# Revit family: NBS_HeatraeSadia_StrgWtrHtrsElctrc_B3MC3M
name_source: partatom
category: Plumbing Fixtures
revit_build: Autodesk Revit 2014 (Build: 20130709_2115(x64)
units: mm (PartAtom-declared; Revit-internal decimal feet)

## types (2) — shared parameters
Accessories = Telescopic spout (95:970:103)
Arrangement = Single point – mains supply
AssetType = Fixed
CW Connection = Yes
CasingFinish = White stove enamel
Color = White
Connections = 15 mm copper pipe connections for cold water inlet and hot water outlet at the base of the unit, vent at the top
Controls = Valve
Depth = 352 mm  [stored 1.15486 ft]
Description = Vented point of use storage water heater
DurationUnit = year
Features = Element ‘on’ indicator, supplied complete with open outlet spout
Fixing = Wall fixed
FlowRate = To suit draw off requirements
HW Connection = No
HeatTransferSurfaceArea = 0
IfcExportAs = IfcBoilerType
IfcExportType = WATER
IsWaterStorageHeater = Yes
ManufacturerName = Heatrae Sadia
ManufacturerURL = www.heatraesadia.com
Material = Outer casing: Plastic top and bottom moulding with corrosion proof steel centre section; Water container: Heavy gauge copper; Heat unit: Replaceable embedded rod-type element sheathed in corrosion resistant alloy
NBSCertification = http://www.nationalbimlibrary.com
NBSDescription = Storage water heaters, electric
NBSReference = 90-15-35/440
NominalLength = 352 mm  [stored 1.15486 ft]
NominalWidth = 370 mm  [stored 1.21391 ft]
OutletTemperatureRange = 5, 75
PartialLoadEfficiencyCurves = 0
PressureRating = 0
ProductInformation = www.heatraesadia.com/docs/344_084_POU-Vented_lit-AW_online.pdf
Rating = 3 kW
SafetyFeatures = Re-settable over temperature cut-out
SpoutProjection = 399 mm
StorageWaterHeaterMaterial = NBS_Concept
ThermalInsulation = CFC/HCFC free (ODP zero) flame-retardant expanded polyurethane
ThirdPartyCertification = Kiwa approved
Uniclass2 = 90-90-46/428
Uniclass2015Description = Electric storage water heaters
Uniclass2015Reference = Pr_60_60_96_28
Uniclass2015Version = Products v1.1
Vent Connection = No
Version = 1
WarrantyDurationParts = 2
WarrantyDurationUnit = year
WarrantyStartDate = 1900-12-31T23:59:59
Waste Connection = No
WaterInletTemperatureRange = 0
Width = 370 mm  [stored 1.21391 ft]
zero-valued in all types: HeatOutput, NominalEfficiency, NominalEnergyConsumption, NominalPartLoadRatio

## per-type parameters (varying)
| type | BIMObjectName | BodyHeight | Height | ModelNumber | ModelReference | Name | NominalHeight | Size | WaterStorageCapacity | Weight |
| B3M30Litre | NBS_HeatraeSadia_StorageWaterHeatersElectric_B3M30Litre | 616 mm  [stored 2.021 ft] | 868 mm  [stored 2.84777 ft] | 95:030:103 | B3M 30 Litre | StorageWaterHeatersElectric_B3M30Litre_HeatraeSadia | 868 mm  [stored 2.84777 ft] | 868 x 370 x 352 mm | 30 | 42.5 |
| C3M50Litre | NBS_HeatraeSadia_StorageWaterHeatersElectric_C3M50Litre | 886 mm  [stored 2.90682 ft] | 1138 mm  [stored 3.7336 ft] | 95:030:104 | C3M 50 Litre | StorageWaterHeatersElectric_C3M50Litre_HeatraeSadia | 1138 mm  [stored 3.7336 ft] | 1138 x 370 x 352 mm | 50 | 69.3 |

note: [stored X ft] marks values corroborated as IEEE doubles in the binary element streams (Revit-internal decimal feet)

## geometry (parser evidence)
native form markers: Blend x13, Sweep x1
no freeform markers — native parametric forms only
